# Revit family: Jardinera Olea
name_source: partatom
category: Furniture
units: mm (PartAtom-declared; Revit-internal decimal feet)

## family parameters
Always vertical = Yes
Cut with Voids When Loaded = No
OmniClass Number = 23.40.20.00
OmniClass Title = General Furniture and Specialties
Room Calculation Point = No
Shared = No
Work Plane-Based = No

## types (2) — shared parameters
A = 0.75 m
H = 0.75 m
zero-valued in all types: Default Elevation

## per-type parameters (varying)
| type | B | Description | Fabricante | Ficha_Tecnica | Material | Referencia | Type Comments | URL_Producto |
| Jardinera Olea-UM1160-750mm | 0 m |  |  |  | <By Category> |  |  |  |
| Jardinera Olea-UM1220-750mm | 0.75 m | Jardinera fabricada en chapa de acero corten, concebida para permanecer en el tiempo sin ningún tipo de mantenimiento. | BENITO URBAN SL | https://www.benito.com | Acero corten | UM1220 | No necesita ningún acabado, evita procesos contaminantes y contribuye a la sostenibilidad medioambiental | https://www.benito.com |

type visibility flags: 2 boolean params named "<type name>" — each type sets only its own to Yes (folded from table)

## geometry (parser evidence)
native form markers: Blend x6, Sweep x6
no freeform markers — native parametric forms only
